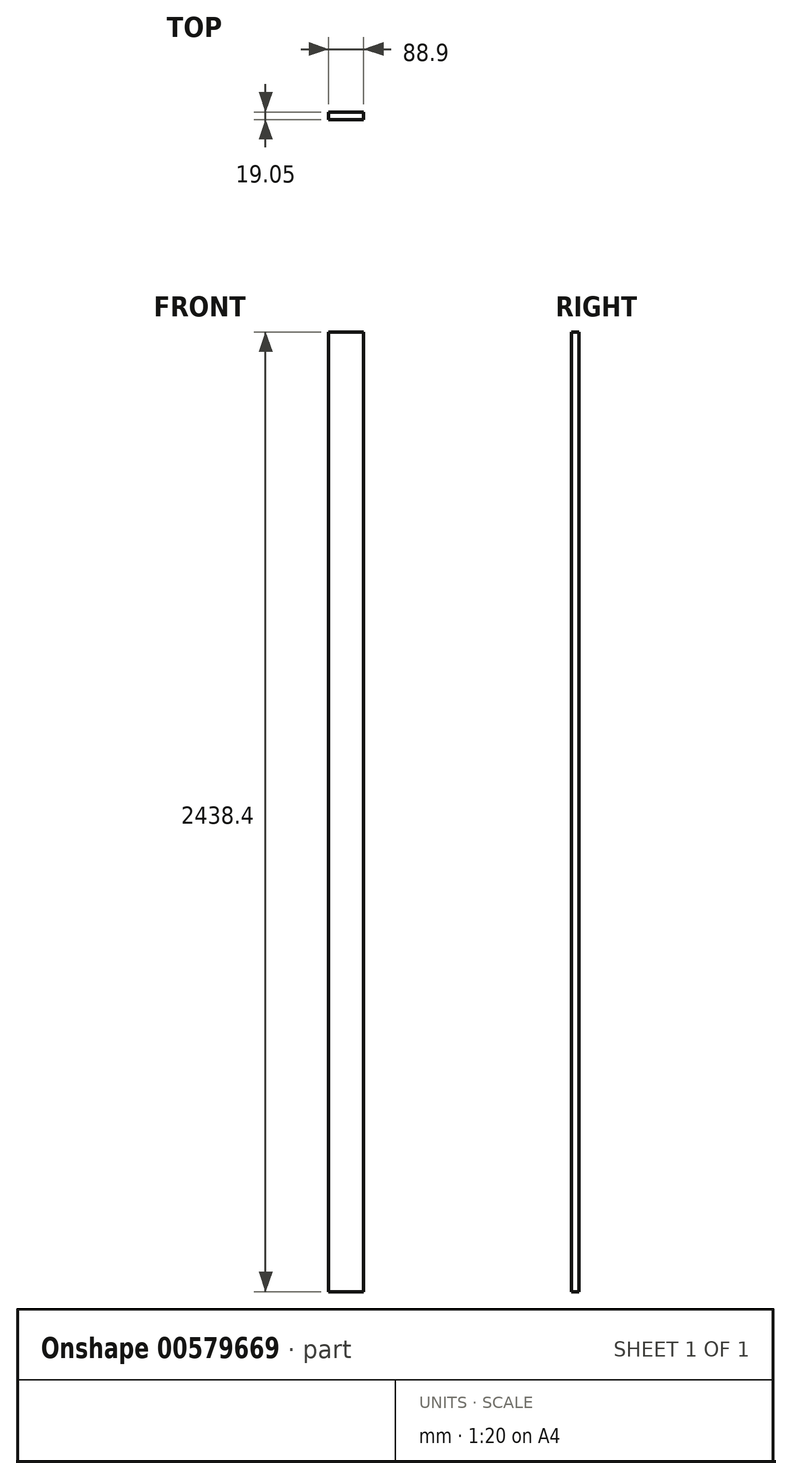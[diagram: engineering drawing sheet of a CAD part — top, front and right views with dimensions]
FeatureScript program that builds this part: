
annotation { "Feature Type Name" : "Feature", "Feature Type Description" : "" }
export const myFeature = defineFeature(function(context is Context, id is Id, definition is map)
    precondition{}
    {
        {
            var Q0;
            Q0=qCreatedBy(makeId("Front.planeOp"),FACE);
            var sketch = newSketch(context, id + "F0", { "sketchPlane" : qUnion([Q0])});
            skLineSegment(sketch, "E0.bottom", {"start": v(44.45, 1219.2) * mm, "end": v(-44.45, 1219.2) * mm});
            skLineSegment(sketch, "E0.top", {"start": v(44.45, -1219.2) * mm, "end": v(-44.45, -1219.2) * mm});
            skLineSegment(sketch, "E0.left", {"start": v(44.45, 1219.2) * mm, "end": v(44.45, -1219.2) * mm});
            skLineSegment(sketch, "E0.right", {"start": v(-44.45, 1219.2) * mm, "end": v(-44.45, -1219.2) * mm});
            skPoint(sketch, "E0.middle", {"position": v(0, 0) * mm});
            skSolve(sketch);
        }
        {
            var Q0;
            Q0 = qSketchRegion(id + "F0", true);
            extrude(context, id + "F1", {"entities" : qUnion([Q0]), "depth" : 19.05 * mm, "offsetDistance" : 25.4 * mm});
        }
    });
